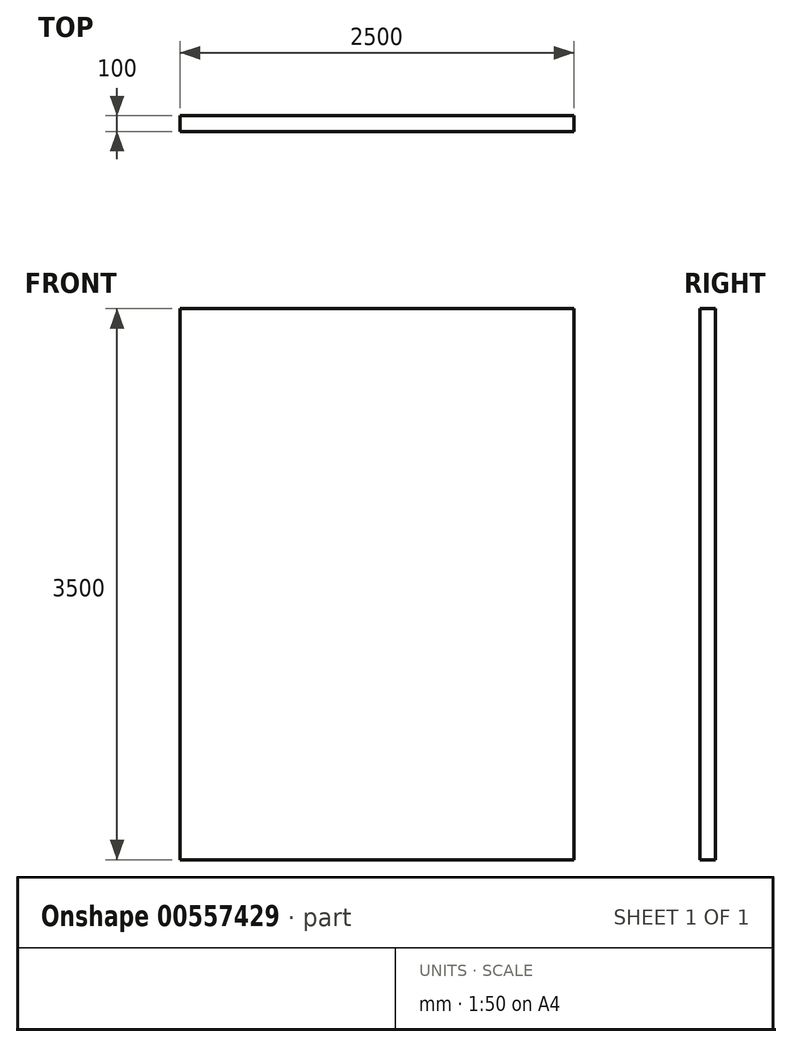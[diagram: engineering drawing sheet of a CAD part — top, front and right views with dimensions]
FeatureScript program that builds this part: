
annotation { "Feature Type Name" : "Feature", "Feature Type Description" : "" }
export const myFeature = defineFeature(function(context is Context, id is Id, definition is map)
    precondition{}
    {
        {
            var Q0;
            Q0=qCreatedBy(makeId("Front.planeOp"),FACE);
            var sketch = newSketch(context, id + "F0", { "sketchPlane" : qUnion([Q0])});
            skLineSegment(sketch, "E0.bottom", {"start": v(1250, 1750) * mm, "end": v(-1250, 1750) * mm});
            skLineSegment(sketch, "E0.top", {"start": v(1250, -1750) * mm, "end": v(-1250, -1750) * mm});
            skLineSegment(sketch, "E0.left", {"start": v(1250, 1750) * mm, "end": v(1250, -1750) * mm});
            skLineSegment(sketch, "E0.right", {"start": v(-1250, 1750) * mm, "end": v(-1250, -1750) * mm});
            skPoint(sketch, "E0.middle", {"position": v(0, 0) * mm});
            skSolve(sketch);
        }
        {
            var Q0;
            Q0=makeQuery(id+"F0.imprint","IMPRINT",FACE,{"disambiguationData":[TD([[makeQuery(id+"F0.imprint","IMPRINT",EDGE,{"derivedFrom":sQuery(id+"F0.wireOp",EDGE,"E0.bottom")}),1.0]])]});
            extrude(context, id + "F1", {"entities" : qUnion([Q0]), "endBound" : BoundingType.SYMMETRIC, "depth" : 100 * mm, "offsetDistance" : 25 * mm});
        }
    });
